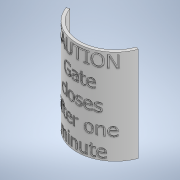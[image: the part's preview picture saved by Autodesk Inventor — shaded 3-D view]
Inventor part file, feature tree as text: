
AUTODESK INVENTOR PART (.ipt)
format: ipt  version: 2021.2 (Build 252289000, 289)  size: 1,515,008 bytes
history: native  units: in
note: dims shown in document units (in); Inventor stores cm internally (conversion verified against a paired STEP export)
features: sketch x2, extrude x1, plane x1, emboss x1
ambient origin geometry x8: Origin, YZ Plane, XZ Plane, XY Plane, X Axis, Y Axis, Z Axis, Center Point
bodies: Solid1 (feature_tree)
feature tree (5):
  extrude  "Extrusion1"  Depth=8.0in TaperAngle=0.0deg
  plane  "Work Plane1"
  emboss  "Emboss1"
  sketch  "Sketch1"  dims[d0=6.0in d2=8.0in d3=0.0in]
  sketch  "Sketch3"  dims[d6=1.0in d7=0.1in d8=0.0in d9=0.25in d10=0.7559in d11=0.7559in]
